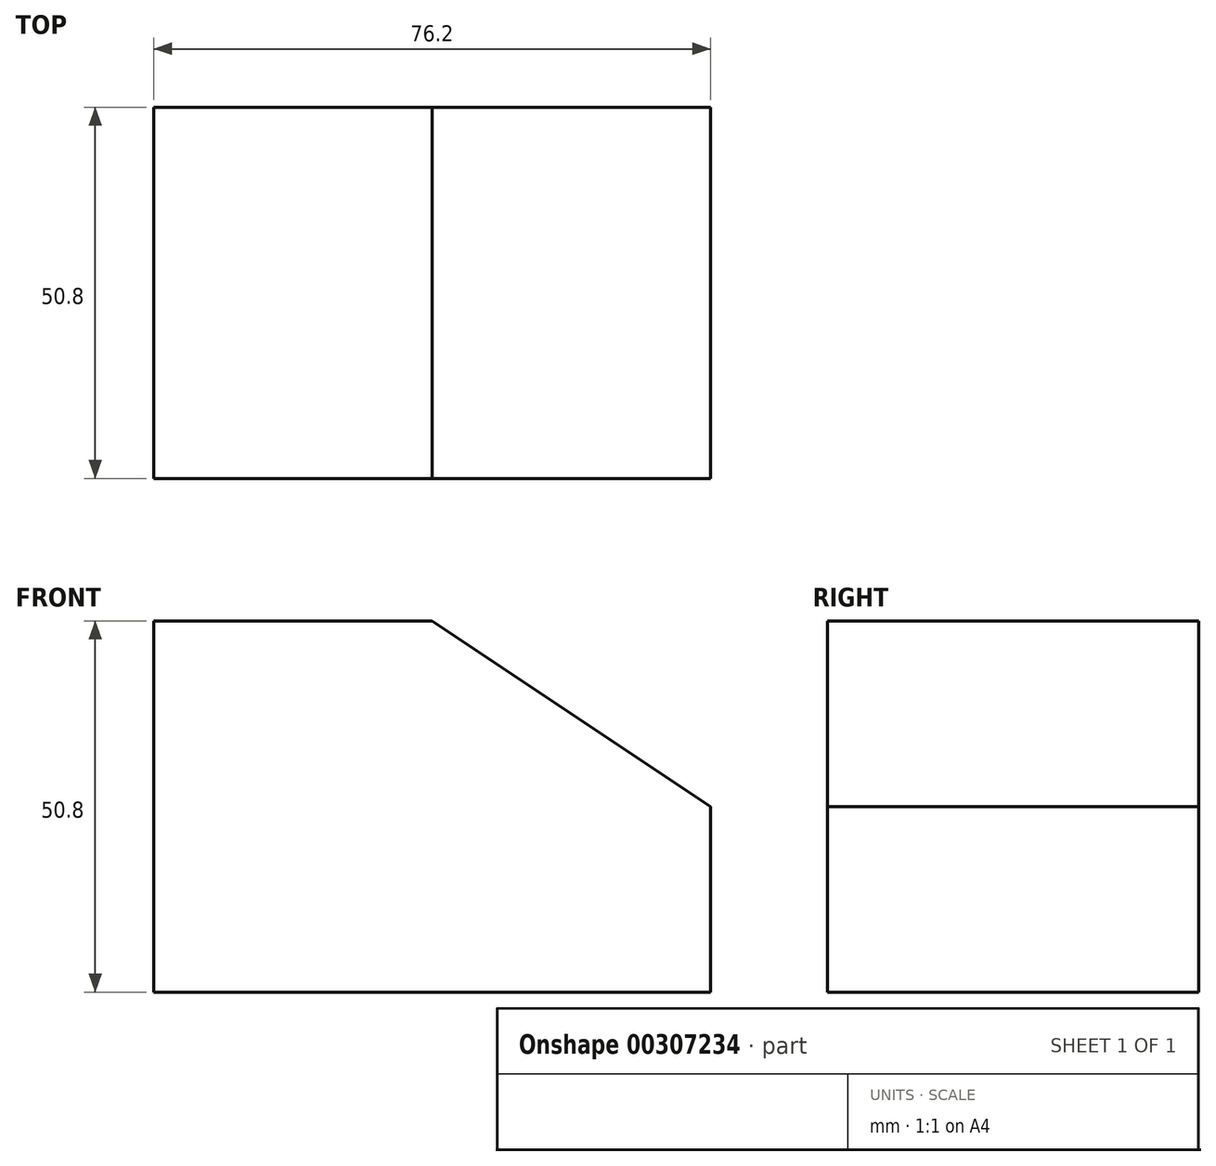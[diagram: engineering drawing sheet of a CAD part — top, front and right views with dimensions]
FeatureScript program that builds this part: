
annotation { "Feature Type Name" : "Feature", "Feature Type Description" : "" }
export const myFeature = defineFeature(function(context is Context, id is Id, definition is map)
    precondition{}
    {
        {
            var Q0;
            Q0=qCreatedBy(makeId("Front.planeOp"),FACE);
            var sketch = newSketch(context, id + "F0", { "sketchPlane" : qUnion([Q0])});
            skLineSegment(sketch, "E0", {"start": v(-46.3, 30.16) * mm, "end": v(-46.3, -20.64) * mm});
            skLineSegment(sketch, "E1", {"start": v(-46.3, -20.64) * mm, "end": v(29.9, -20.64) * mm});
            skLineSegment(sketch, "E2", {"start": v(-46.3, 30.16) * mm, "end": v(-8.2, 30.16) * mm});
            skLineSegment(sketch, "E3", {"start": v(29.9, -20.64) * mm, "end": v(29.9, 4.76) * mm});
            skLineSegment(sketch, "E4", {"start": v(29.9, 4.76) * mm, "end": v(-8.2, 30.16) * mm});
            skSolve(sketch);
        }
        {
            var Q0;
            Q0 = qSketchRegion(id + "F0", true);
            extrude(context, id + "F1", {"entities" : qUnion([Q0]), "depth" : 50.8 * mm});
        }
    });
